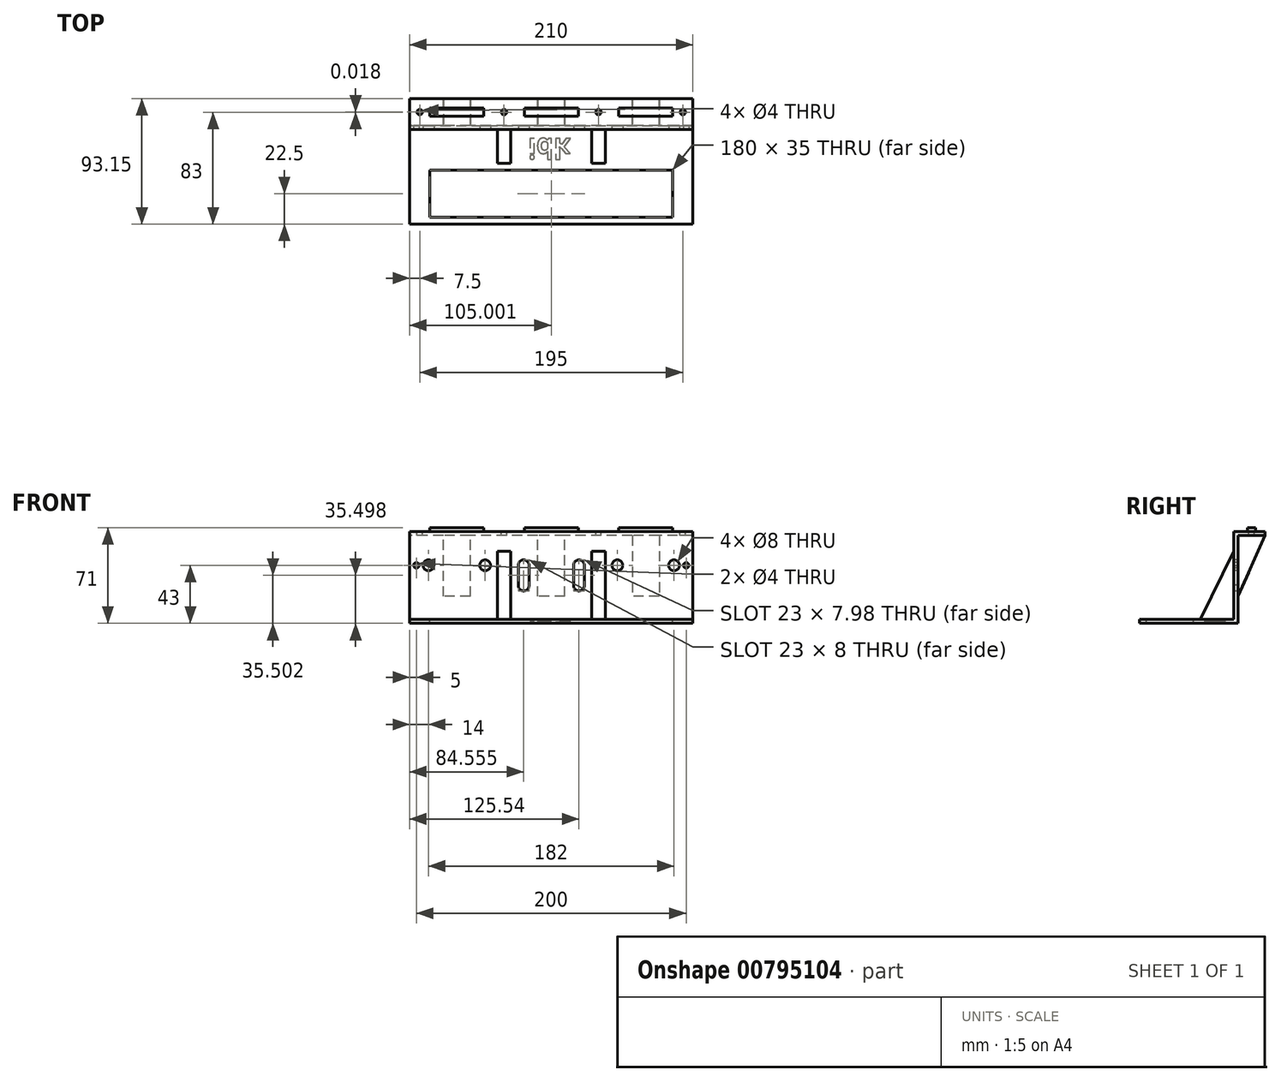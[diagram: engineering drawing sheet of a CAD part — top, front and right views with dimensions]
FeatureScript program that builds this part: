
annotation { "Feature Type Name" : "Feature", "Feature Type Description" : "" }
export const myFeature = defineFeature(function(context is Context, id is Id, definition is map)
    precondition{}
    {
        {
            var Q0;
            Q0=qCreatedBy(makeId("Top.planeOp"),FACE);
            var sketch = newSketch(context, id + "F0", { "sketchPlane" : qUnion([Q0])});
            skLineSegment(sketch, "E0.bottom", {"start": v(105, 0) * mm, "end": v(-105, 0) * mm});
            skLineSegment(sketch, "E0.top", {"start": v(105, 20) * mm, "end": v(-105, 20) * mm});
            skLineSegment(sketch, "E0.left", {"start": v(105, 0) * mm, "end": v(105, 20) * mm});
            skLineSegment(sketch, "E0.right", {"start": v(-105, 0) * mm, "end": v(-105, 20) * mm});
            skPoint(sketch, "E0.middle", {"position": v(0, 10) * mm});
            skSolve(sketch);
        }
        {
            var Q0;
            Q0 = qSketchRegion(id + "F0", true);
            extrude(context, id + "F1", {"entities" : qUnion([Q0]), "depth" : 3 * mm, "offsetDistance" : 25 * mm});
        }
        {
            var Q0;
            Q0=qCreatedBy(makeId("Front.planeOp"),FACE);
            var sketch = newSketch(context, id + "F2", { "sketchPlane" : qUnion([Q0])});
            skLineSegment(sketch, "E1.bottom", {"start": v(-105, 3) * mm, "end": v(105, 3) * mm});
            skLineSegment(sketch, "E1.top", {"start": v(-105, -62) * mm, "end": v(105, -62) * mm});
            skLineSegment(sketch, "E1.left", {"start": v(-105, 3) * mm, "end": v(-105, -62) * mm});
            skLineSegment(sketch, "E1.right", {"start": v(105, 3) * mm, "end": v(105, -62) * mm});
            skSolve(sketch);
        }
        {
            var Q0;
            Q0 = qSketchRegion(id + "F2", true);
            extrude(context, id + "F3", {"entities" : qUnion([Q0]), "operationType" : NewBodyOperationType.ADD, "depth" : 3 * mm, "offsetDistance" : 25 * mm});
        }
        {
            var Q0;
            Q0=qCreatedBy(makeId("Top.planeOp"),FACE);
            cPlane(context, id + "F4", {"entities" : qUnion([Q0]), "cplaneType" : CPlaneType.OFFSET, "offset" : 65 * mm, "oppositeDirection" : true, "width" : 150 * mm, "height" : 150 * mm});
        }
        {
            var Q0;
            Q0=qCreatedBy(id+"F4.planeOp",FACE);
            var sketch = newSketch(context, id + "F5", { "sketchPlane" : qUnion([Q0])});
            skLineSegment(sketch, "E2.bottom", {"start": v(-105, 0) * mm, "end": v(105, 0) * mm});
            skLineSegment(sketch, "E2.top", {"start": v(-105, -73) * mm, "end": v(105, -73) * mm});
            skLineSegment(sketch, "E2.left", {"start": v(-105, 0) * mm, "end": v(-105, -73) * mm});
            skLineSegment(sketch, "E2.right", {"start": v(105, 0) * mm, "end": v(105, -73) * mm});
            skSolve(sketch);
        }
        {
            var Q0;
            Q0 = qSketchRegion(id + "F5", true);
            extrude(context, id + "F6", {"entities" : qUnion([Q0]), "operationType" : NewBodyOperationType.ADD, "depth" : 3 * mm, "offsetDistance" : 25 * mm});
        }
        {
            var Q0;
            Q0=qCreatedBy(makeId("Right.planeOp"),FACE);
            var sketch = newSketch(context, id + "F7", { "sketchPlane" : qUnion([Q0])});
            skLineSegment(sketch, "E3", {"start": v(20.02, 0) * mm, "end": v(0, -45) * mm});
            skLineSegment(sketch, "E4", {"start": v(0, -45) * mm, "end": v(0, 0) * mm});
            skLineSegment(sketch, "E5", {"start": v(0, 0) * mm, "end": v(20.02, 0) * mm});
            skSolve(sketch);
        }
        {
            var Q0;
            Q0 = qSketchRegion(id + "F7", true);
            extrude(context, id + "F8", {"entities" : qUnion([Q0]), "operationType" : NewBodyOperationType.ADD, "depth" : 10 * mm, "offsetDistance" : 25 * mm});
        }
        {
            var Q0;
            Q0=makeQuery(id+"F8.opExtrude","CAP_FACE",FACE,{"disambiguationData":[OSD([sQuery(id+"F7.wireOp",EDGE,"E3"),sQuery(id+"F7.wireOp",EDGE,"E4"),sQuery(id+"F7.wireOp",EDGE,"E5")])],"isStart":true});
            extrude(context, id + "F9", {"entities" : qUnion([Q0]), "operationType" : NewBodyOperationType.ADD, "depth" : 10 * mm, "offsetDistance" : 25 * mm});
        }
        {
            var Q0;
            Q0=qCreatedBy(makeId("Right.planeOp"),FACE);
            var Q1;
            Q1 = qBodyType(qCreatedBy(id + "F12" ,EDGE), BodyType.WIRE);
            cPlane(context, id + "F10", {"entities" : qUnion([Q0, Q1]), "cplaneType" : CPlaneType.OFFSET, "offset" : 70 * mm, "width" : 150 * mm, "height" : 150 * mm});
        }
        {
            var Q0;
            Q0=qCreatedBy(makeId("Right.planeOp"),FACE);
            cPlane(context, id + "F11", {"entities" : qUnion([Q0]), "cplaneType" : CPlaneType.OFFSET, "offset" : 70 * mm, "oppositeDirection" : true, "width" : 150 * mm, "height" : 150 * mm});
        }
        {
            var Q0;
            Q0=qCreatedBy(id+"F10.planeOp",FACE);
            var sketch = newSketch(context, id + "F12", { "sketchPlane" : qUnion([Q0])});
            skSolve(sketch);
        }
        {
            var Q0;
            Q0=qCreatedBy(id+"F11.planeOp",FACE);
            var sketch = newSketch(context, id + "F13", { "sketchPlane" : qUnion([Q0])});
            skLineSegment(sketch, "E6", {"start": v(20.01, 0) * mm, "end": v(0, -45.09) * mm});
            skLineSegment(sketch, "E7", {"start": v(0, -45.09) * mm, "end": v(0, 0) * mm});
            skLineSegment(sketch, "E8", {"start": v(0, 0) * mm, "end": v(20.01, 0) * mm});
            skSolve(sketch);
        }
        {
            var Q0;
            Q0 = qSketchRegion(id + "F13", true);
            extrude(context, id + "F14", {"entities" : qUnion([Q0]), "operationType" : NewBodyOperationType.ADD, "depth" : 10 * mm, "offsetDistance" : 25 * mm});
        }
        {
            var Q0;
            Q0=makeQuery(id+"F14.opExtrude","CAP_FACE",FACE,{"disambiguationData":[OSD([sQuery(id+"F13.wireOp",EDGE,"E6"),sQuery(id+"F13.wireOp",EDGE,"E7"),sQuery(id+"F13.wireOp",EDGE,"E8")])],"isStart":true});
            extrude(context, id + "F15", {"entities" : qUnion([Q0]), "operationType" : NewBodyOperationType.ADD, "depth" : 10 * mm, "offsetDistance" : 25 * mm});
        }
        {
            var Q0;
            Q0=qCreatedBy(id+"F10.planeOp",FACE);
            var sketch = newSketch(context, id + "F16", { "sketchPlane" : qUnion([Q0])});
            skLineSegment(sketch, "E9", {"start": v(0, -44.9) * mm, "end": v(20.15, 0) * mm});
            skLineSegment(sketch, "E10", {"start": v(20.15, 0) * mm, "end": v(0, 0) * mm});
            skLineSegment(sketch, "E11", {"start": v(0, 0) * mm, "end": v(0, -44.9) * mm});
            skSolve(sketch);
        }
        {
            var Q0;
            Q0 = qSketchRegion(id + "F16", true);
            extrude(context, id + "F17", {"entities" : qUnion([Q0]), "operationType" : NewBodyOperationType.ADD, "depth" : 10 * mm, "offsetDistance" : 25 * mm});
        }
        {
            var Q0;
            Q0=makeQuery(id+"F17.opExtrude","CAP_FACE",FACE,{"disambiguationData":[OSD([sQuery(id+"F16.wireOp",EDGE,"E9"),sQuery(id+"F16.wireOp",EDGE,"E10"),sQuery(id+"F16.wireOp",EDGE,"E11")])],"isStart":true});
            extrude(context, id + "F18", {"entities" : qUnion([Q0]), "operationType" : NewBodyOperationType.ADD, "depth" : 10 * mm, "offsetDistance" : 25 * mm});
        }
        {
            var Q0;
            Q0=qCreatedBy(makeId("Right.planeOp"),FACE);
            cPlane(context, id + "F19", {"entities" : qUnion([Q0]), "cplaneType" : CPlaneType.OFFSET, "offset" : 35 * mm, "width" : 150 * mm, "height" : 150 * mm});
        }
        {
            var Q0;
            Q0=qCreatedBy(makeId("Right.planeOp"),FACE);
            cPlane(context, id + "F20", {"entities" : qUnion([Q0]), "cplaneType" : CPlaneType.OFFSET, "offset" : 35 * mm, "oppositeDirection" : true, "width" : 150 * mm, "height" : 150 * mm});
        }
        {
            var Q0;
            Q0=qCreatedBy(id+"F20.planeOp",FACE);
            var sketch = newSketch(context, id + "F21", { "sketchPlane" : qUnion([Q0])});
            skLineSegment(sketch, "E12", {"start": v(-3, -11.5) * mm, "end": v(-3, -62) * mm});
            skLineSegment(sketch, "E13", {"start": v(-3, -62) * mm, "end": v(-28, -62) * mm});
            skLineSegment(sketch, "E14", {"start": v(-28, -62) * mm, "end": v(-3, -11.5) * mm});
            skSolve(sketch);
        }
        {
            var Q0;
            Q0 = qSketchRegion(id + "F21", true);
            extrude(context, id + "F22", {"entities" : qUnion([Q0]), "depth" : 5 * mm, "offsetDistance" : 25 * mm});
        }
        {
            var Q0;
            Q0=makeQuery(id+"F22.opExtrude","CAP_FACE",FACE,{"disambiguationData":[OSD([sQuery(id+"F21.wireOp",EDGE,"E12"),sQuery(id+"F21.wireOp",EDGE,"E13"),sQuery(id+"F21.wireOp",EDGE,"E14")])],"isStart":true});
            extrude(context, id + "F23", {"entities" : qUnion([Q0]), "operationType" : NewBodyOperationType.ADD, "depth" : 5 * mm, "offsetDistance" : 25 * mm});
        }
        {
            var Q0;
            Q0=qCreatedBy(id+"F19.planeOp",FACE);
            var sketch = newSketch(context, id + "F24", { "sketchPlane" : qUnion([Q0])});
            skLineSegment(sketch, "E15", {"start": v(-3, -62) * mm, "end": v(-3, -11.5) * mm});
            skLineSegment(sketch, "E16", {"start": v(-3, -11.5) * mm, "end": v(-28, -62) * mm});
            skLineSegment(sketch, "E17", {"start": v(-28, -62) * mm, "end": v(-3, -62) * mm});
            skSolve(sketch);
        }
        {
            var Q0;
            Q0 = qSketchRegion(id + "F24", true);
            extrude(context, id + "F25", {"entities" : qUnion([Q0]), "depth" : 5 * mm, "offsetDistance" : 25 * mm});
        }
        {
            var Q0;
            Q0=makeQuery(id+"F25.opExtrude","CAP_FACE",FACE,{"disambiguationData":[OSD([sQuery(id+"F24.wireOp",EDGE,"E15"),sQuery(id+"F24.wireOp",EDGE,"E16"),sQuery(id+"F24.wireOp",EDGE,"E17")])],"isStart":true});
            extrude(context, id + "F26", {"entities" : qUnion([Q0]), "operationType" : NewBodyOperationType.ADD, "depth" : 5 * mm, "offsetDistance" : 25 * mm});
        }
        {
            var Q0;
            Q0=qCreatedBy(makeId("Top.planeOp"),FACE);
            var sketch = newSketch(context, id + "F27", { "sketchPlane" : qUnion([Q0])});
            skLineSegment(sketch, "E18.bottom", {"start": v(90, 7) * mm, "end": v(50, 7) * mm});
            skLineSegment(sketch, "E18.top", {"start": v(90, 13) * mm, "end": v(50, 13) * mm});
            skLineSegment(sketch, "E18.left", {"start": v(90, 7) * mm, "end": v(90, 13) * mm});
            skLineSegment(sketch, "E18.right", {"start": v(50, 7) * mm, "end": v(50, 13) * mm});
            skPoint(sketch, "E18.middle", {"position": v(70, 10) * mm});
            skLineSegment(sketch, "E19.bottom", {"start": v(20, 7) * mm, "end": v(-20, 7) * mm});
            skLineSegment(sketch, "E19.top", {"start": v(20, 13) * mm, "end": v(-20, 13) * mm});
            skLineSegment(sketch, "E19.left", {"start": v(20, 7) * mm, "end": v(20, 13) * mm});
            skLineSegment(sketch, "E19.right", {"start": v(-20, 7) * mm, "end": v(-20, 13) * mm});
            skPoint(sketch, "E19.middle", {"position": v(0, 10) * mm});
            skLineSegment(sketch, "E20.bottom", {"start": v(-50, 7) * mm, "end": v(-90, 7) * mm});
            skLineSegment(sketch, "E20.top", {"start": v(-50, 13) * mm, "end": v(-90, 13) * mm});
            skLineSegment(sketch, "E20.left", {"start": v(-50, 7) * mm, "end": v(-50, 13) * mm});
            skLineSegment(sketch, "E20.right", {"start": v(-90, 7) * mm, "end": v(-90, 13) * mm});
            skPoint(sketch, "E20.middle", {"position": v(-70, 10) * mm});
            skCircle(sketch, "E21", {"center": v(35, 10) * mm, "radius": 2 * mm});
            skCircle(sketch, "E22", {"center": v(-35, 10) * mm, "radius": 2 * mm});
            skCircle(sketch, "E23", {"center": v(-97.5, 10) * mm, "radius": 2 * mm});
            skCircle(sketch, "E24", {"center": v(97.5, 10) * mm, "radius": 2 * mm});
            skSolve(sketch);
        }
        {
            var Q0;
            Q0=makeQuery(id+"F27.imprint","IMPRINT",FACE,{"disambiguationData":[TD([[makeQuery(id+"F27.imprint","IMPRINT",EDGE,{"derivedFrom":sQuery(id+"F27.wireOp",EDGE,"E20.bottom")}),-1.0]])]});
            var Q1;
            Q1=makeQuery(id+"F27.imprint","IMPRINT",FACE,{"disambiguationData":[TD([[makeQuery(id+"F27.imprint","IMPRINT",EDGE,{"derivedFrom":sQuery(id+"F27.wireOp",EDGE,"E19.bottom")}),-1.0]])]});
            var Q2;
            Q2=makeQuery(id+"F27.imprint","IMPRINT",FACE,{"disambiguationData":[TD([[makeQuery(id+"F27.imprint","IMPRINT",EDGE,{"derivedFrom":sQuery(id+"F27.wireOp",EDGE,"E18.bottom")}),-1.0]])]});
            extrude(context, id + "F28", {"entities" : qUnion([Q0, Q1, Q2]), "operationType" : NewBodyOperationType.ADD, "depth" : 6 * mm, "offsetDistance" : 25 * mm});
        }
        {
            var Q0;
            Q0=makeQuery(id+"F1.opExtrude","CAP_FACE",FACE,{"disambiguationData":[OSD([sQuery(id+"F0.wireOp",EDGE,"E0.bottom"),sQuery(id+"F0.wireOp",EDGE,"E0.top"),sQuery(id+"F0.wireOp",EDGE,"E0.left"),sQuery(id+"F0.wireOp",EDGE,"E0.right")])],"isStart":false});
            var sketch = newSketch(context, id + "F29", { "sketchPlane" : qUnion([Q0])});
            skPoint(sketch, "E25.middle", {"position": v(70, 0) * mm});
            skPoint(sketch, "E26.middle", {"position": v(0, 0) * mm});
            skPoint(sketch, "E27.middle", {"position": v(-70, 0) * mm});
            skCircle(sketch, "E28", {"center": v(35, 10) * mm, "radius": 2 * mm});
            skCircle(sketch, "E29", {"center": v(-35, 10) * mm, "radius": 2 * mm});
            skCircle(sketch, "E30", {"center": v(-97.5, 10.02) * mm, "radius": 2 * mm});
            skCircle(sketch, "E31", {"center": v(97.5, 10) * mm, "radius": 2 * mm});
            skSolve(sketch);
        }
        {
            var Q0;
            Q0=makeQuery(id+"F29.imprint","IMPRINT",FACE,{"disambiguationData":[TD([[makeQuery(id+"F29.imprint","IMPRINT",EDGE,{"derivedFrom":sQuery(id+"F29.wireOp",EDGE,"E29")}),1.0]])]});
            var Q1;
            Q1=makeQuery(id+"F29.imprint","IMPRINT",FACE,{"disambiguationData":[TD([[makeQuery(id+"F29.imprint","IMPRINT",EDGE,{"derivedFrom":sQuery(id+"F29.wireOp",EDGE,"E30")}),1.0]])]});
            var Q2;
            Q2=makeQuery(id+"F29.imprint","IMPRINT",FACE,{"disambiguationData":[TD([[makeQuery(id+"F29.imprint","IMPRINT",EDGE,{"derivedFrom":sQuery(id+"F29.wireOp",EDGE,"E28")}),1.0]])]});
            var Q3;
            Q3=makeQuery(id+"F29.imprint","IMPRINT",FACE,{"disambiguationData":[TD([[makeQuery(id+"F29.imprint","IMPRINT",EDGE,{"derivedFrom":sQuery(id+"F29.wireOp",EDGE,"E31")}),1.0]])]});
            extrude(context, id + "F30", {"entities" : qUnion([Q0, Q1, Q2, Q3]), "operationType" : NewBodyOperationType.REMOVE, "oppositeDirection" : true, "depth" : 3 * mm, "offsetDistance" : 25 * mm});
        }
        {
            var Q0;
            Q0=makeQuery(id+"F6.opExtrude","CAP_FACE",FACE,{"disambiguationData":[OSD([sQuery(id+"F5.wireOp",EDGE,"E2.bottom"),sQuery(id+"F5.wireOp",EDGE,"E2.top"),sQuery(id+"F5.wireOp",EDGE,"E2.left"),sQuery(id+"F5.wireOp",EDGE,"E2.right")])],"isStart":false});
            var sketch = newSketch(context, id + "F31", { "sketchPlane" : qUnion([Q0])});
            skLineSegment(sketch, "E32.bottom", {"start": v(90, -68) * mm, "end": v(-90, -68) * mm});
            skLineSegment(sketch, "E32.top", {"start": v(90, -33) * mm, "end": v(-90, -33) * mm});
            skLineSegment(sketch, "E32.left", {"start": v(90, -68) * mm, "end": v(90, -33) * mm});
            skLineSegment(sketch, "E32.right", {"start": v(-90, -68) * mm, "end": v(-90, -33) * mm});
            skPoint(sketch, "E32.middle", {"position": v(0, -50.5) * mm});
            skPoint(sketch, "E32.middle.positionSnap0", {"position": v(0, -73) * mm});
            skPoint(sketch, "E32.centerSnap0", {"position": v(0, -73) * mm});
            skSolve(sketch);
        }
        {
            var Q0;
            Q0 = qSketchRegion(id + "F31", true);
            extrude(context, id + "F32", {"entities" : qUnion([Q0]), "operationType" : NewBodyOperationType.REMOVE, "oppositeDirection" : true, "depth" : 3 * mm, "offsetDistance" : 25 * mm});
        }
        {
            var Q0;
            Q0=makeQuery(id+"F3.opExtrude","CAP_FACE",FACE,{"disambiguationData":[OSD([sQuery(id+"F2.wireOp",EDGE,"E1.bottom"),sQuery(id+"F2.wireOp",EDGE,"E1.top"),sQuery(id+"F2.wireOp",EDGE,"E1.left"),sQuery(id+"F2.wireOp",EDGE,"E1.right")])],"isStart":false});
            var sketch = newSketch(context, id + "F33", { "sketchPlane" : qUnion([Q0])});
            skCircle(sketch, "E33", {"center": v(-91, -22) * mm, "radius": 4 * mm});
            skCircle(sketch, "E34", {"center": v(91, -22) * mm, "radius": 4 * mm});
            skPoint(sketch, "E35.middle", {"position": v(0, -5) * mm});
            skCircle(sketch, "E36", {"center": v(-49, -22) * mm, "radius": 4 * mm});
            skCircle(sketch, "E37", {"center": v(49, -22) * mm, "radius": 4 * mm});
            skCircle(sketch, "E38", {"center": v(-100, -22) * mm, "radius": 2 * mm});
            skCircle(sketch, "E39", {"center": v(100, -22) * mm, "radius": 2 * mm});
            skCircle(sketch, "E40", {"center": v(-20.44, -22) * mm, "radius": 4 * mm});
            skCircle(sketch, "E41", {"center": v(-20.44, -37) * mm, "radius": 4 * mm});
            skLineSegment(sketch, "E42", {"start": v(-24.43, -21.67) * mm, "end": v(-24.44, -37) * mm});
            skLineSegment(sketch, "E43", {"start": v(-16.44, -22) * mm, "end": v(-16.44, -37) * mm});
            skCircle(sketch, "E44", {"center": v(20.53, -22) * mm, "radius": 4 * mm});
            skCircle(sketch, "E45", {"center": v(20.53, -37) * mm, "radius": 4 * mm});
            skLineSegment(sketch, "E46", {"start": v(16.55, -21.62) * mm, "end": v(16.55, -37.36) * mm});
            skLineSegment(sketch, "E47", {"start": v(24.52, -21.73) * mm, "end": v(24.53, -37.36) * mm});
            skSolve(sketch);
        }
        {
            var Q0;
            Q0 = qSketchRegion(id + "F33", true);
            extrude(context, id + "F34", {"entities" : qUnion([Q0]), "operationType" : NewBodyOperationType.REMOVE, "oppositeDirection" : true, "depth" : 3 * mm, "offsetDistance" : 25 * mm});
        }
        {
            var Q0;
            Q0=makeQuery(id+"F6.opExtrude","CAP_FACE",FACE,{"disambiguationData":[OSD([sQuery(id+"F5.wireOp",EDGE,"E2.bottom"),sQuery(id+"F5.wireOp",EDGE,"E2.top"),sQuery(id+"F5.wireOp",EDGE,"E2.left"),sQuery(id+"F5.wireOp",EDGE,"E2.right")])],"isStart":true});
            var sketch = newSketch(context, id + "F35", { "sketchPlane" : qUnion([Q0])});
            skText(sketch, "E48", { "text": "idk", "fontName": "OpenSans-Bold.ttf"});
            const initialGuessF35  = {"E48": [-0.01737, 0.00945, 1, 0, 0.0147]};
            skSetInitialGuess(sketch, initialGuessF35);
            skSolve(sketch);
        }
        {
            var Q0;
            Q0 = qSketchRegion(id + "F35", true);
            extrude(context, id + "F36", {"entities" : qUnion([Q0]), "operationType" : NewBodyOperationType.REMOVE, "oppositeDirection" : true, "depth" : 1 * mm, "offsetDistance" : 25 * mm});
        }
    });
